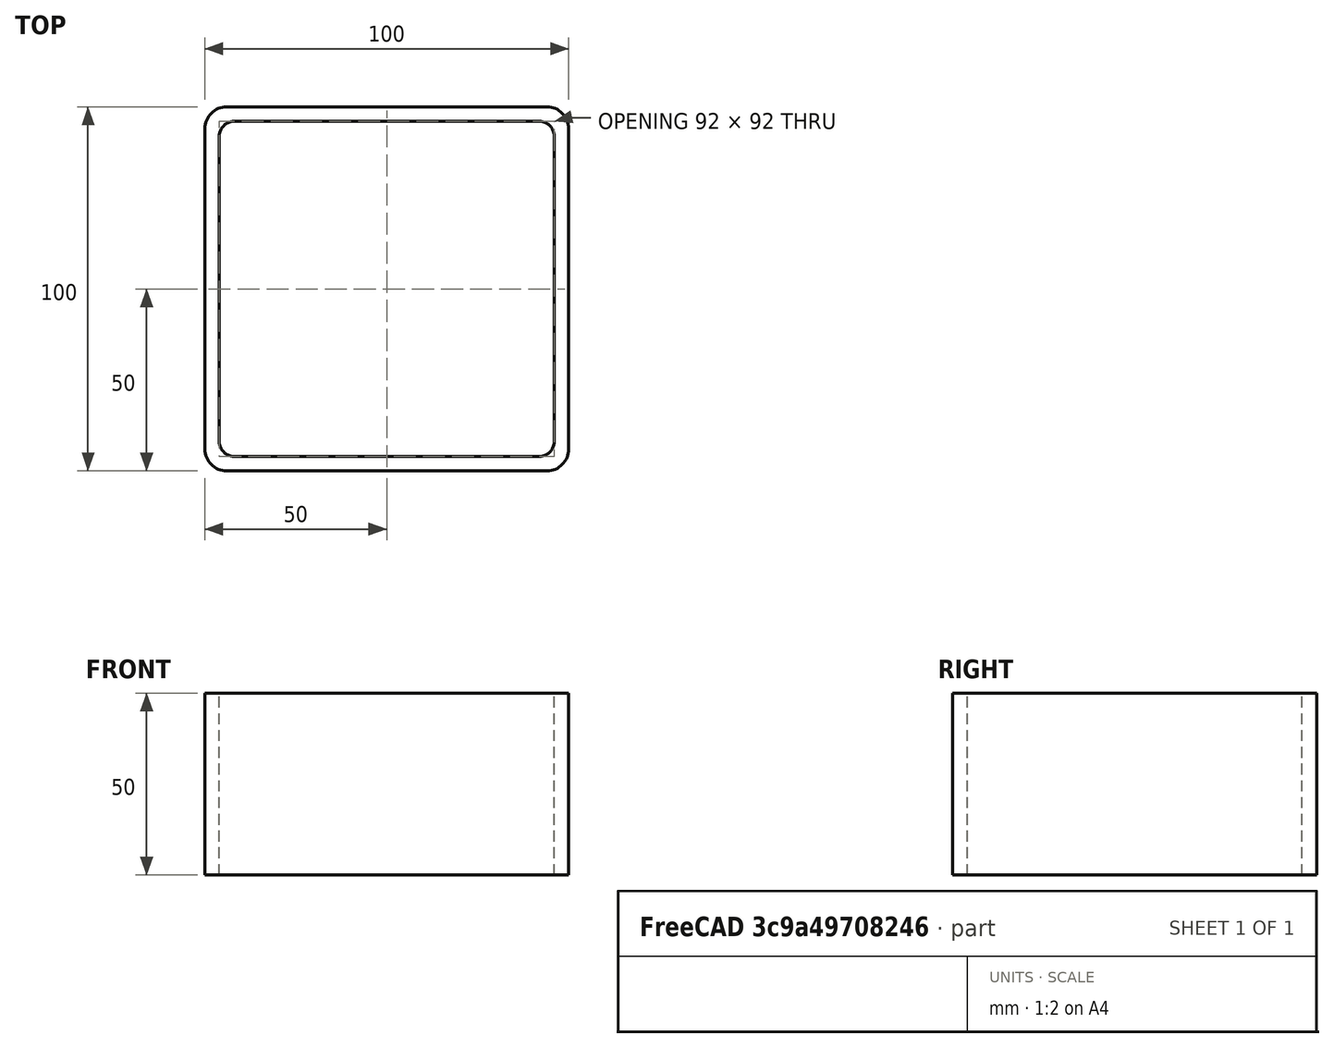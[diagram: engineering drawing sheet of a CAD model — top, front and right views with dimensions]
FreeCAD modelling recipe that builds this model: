
FCSTD DOCUMENT  (FreeCAD 0.15R4671 (Git))
Label: Square hollow section 100x100x4 EN10219 S235JRH
License: All rights reserved
LicenseURL: http://en.wikipedia.org/wiki/All_rights_reserved
objects: Sketcher::SketchObject×1, Part::Extrusion×1
note: 2 computed .brp shape members not serialized (recipe doc carries the construction recipe); baked Part::Feature solids carry a one-line shape summary decoded from their .brp

FEATURE [Sketcher::SketchObject] Sketch
  sketch-geometry (16):
    g0: LineSegment StartX=-42 StartY=46 StartZ=0 EndX=42 EndY=46 EndZ=0
    g1: LineSegment StartX=46 StartY=42 StartZ=0 EndX=46 EndY=-42 EndZ=0
    g2: LineSegment StartX=42 StartY=-46 StartZ=0 EndX=-42 EndY=-46 EndZ=0
    g3: LineSegment StartX=-46 StartY=-42 StartZ=0 EndX=-46 EndY=42 EndZ=0
    g4: LineSegment StartX=-44 StartY=50 StartZ=0 EndX=44 EndY=50 EndZ=0
    g5: LineSegment StartX=50 StartY=44 StartZ=0 EndX=50 EndY=-44 EndZ=0
    g6: LineSegment StartX=44 StartY=-50 StartZ=0 EndX=-44 EndY=-50 EndZ=0
    g7: LineSegment StartX=-50 StartY=-44 StartZ=0 EndX=-50 EndY=44 EndZ=0
    g8: ArcOfCircle CenterX=-42 CenterY=42 CenterZ=0 NormalX=0 NormalY=0 NormalZ=1 Radius=4 StartAngle=1.5708 EndAngle=3.14159
    g9: ArcOfCircle CenterX=42 CenterY=42 CenterZ=0 NormalX=0 NormalY=0 NormalZ=1 Radius=4 StartAngle=0 EndAngle=1.5708
    g10: ArcOfCircle CenterX=42 CenterY=-42 CenterZ=0 NormalX=0 NormalY=0 NormalZ=1 Radius=4 StartAngle=4.71239 EndAngle=6.28319
    g11: ArcOfCircle CenterX=-42 CenterY=-42 CenterZ=0 NormalX=0 NormalY=0 NormalZ=1 Radius=4 StartAngle=3.14159 EndAngle=4.71239
    g12: ArcOfCircle CenterX=44 CenterY=44 CenterZ=0 NormalX=0 NormalY=0 NormalZ=1 Radius=6 StartAngle=0 EndAngle=1.5708
    g13: ArcOfCircle CenterX=44 CenterY=-44 CenterZ=0 NormalX=0 NormalY=0 NormalZ=1 Radius=6 StartAngle=4.71239 EndAngle=6.28319
    g14: ArcOfCircle CenterX=-44 CenterY=-44 CenterZ=0 NormalX=0 NormalY=0 NormalZ=1 Radius=6 StartAngle=3.14159 EndAngle=4.71239
    g15: ArcOfCircle CenterX=-44 CenterY=44 CenterZ=0 NormalX=0 NormalY=0 NormalZ=1 Radius=6 StartAngle=1.5708 EndAngle=3.14159
  constraints (36):
    c: Horizontal(g2)
    c: Vertical(g3)
    c: Horizontal(g6)
    c: Vertical(g7)
    c: Tangent(g3,g8) = 1.5708
    c: Tangent(g0,g8) = 1.5708
    c: Tangent(g0,g9) = 1.5708
    c: Tangent(g1,g9) = 1.5708
    c: Tangent(g1,g10) = 1.5708
    c: Tangent(g2,g10) = 1.5708
    c: Tangent(g2,g11) = 1.5708
    c: Tangent(g3,g11) = 1.5708
    c: Tangent(g4,g12) = 1.5708
    c: Tangent(g5,g12) = 1.5708
    c: Tangent(g5,g13) = 1.5708
    c: Tangent(g6,g13) = 1.5708
    c: Tangent(g6,g14) = 1.5708
    c: Tangent(g7,g14) = 1.5708
    c: Tangent(g7,g15) = 1.5708
    c: Tangent(g4,g15) = 1.5708
    c: Equal(g9,g8)
    c: Equal(g9,g11)
    c: Equal(g9,g10)
    c: Equal(g12,g15)
    c: Equal(g12,g14)
    c: Equal(g12,g13)
    c: Symmetric(g4,g6,g-1)
    c: Symmetric(g7,g5,g-2)
    c: DistanceY(g4,g6) = -100
    c: DistanceX(g7,g5) = 100
    c: Symmetric(g3,g1,g-2)
    c: Symmetric(g0,g2,g-1)
    c: DistanceY(g0,g4) = 4
    c: DistanceX(g5,g1) = -4
    c: Radius(g9) = 4
    c: Radius(g12) = 6
FEATURE [Part::Extrusion] Extrude  label="Square hollow section 100x100x4 EN10219 S235JRH"
  Base = -> Sketch
  Dir = (0,0,50)
  Solid = true
